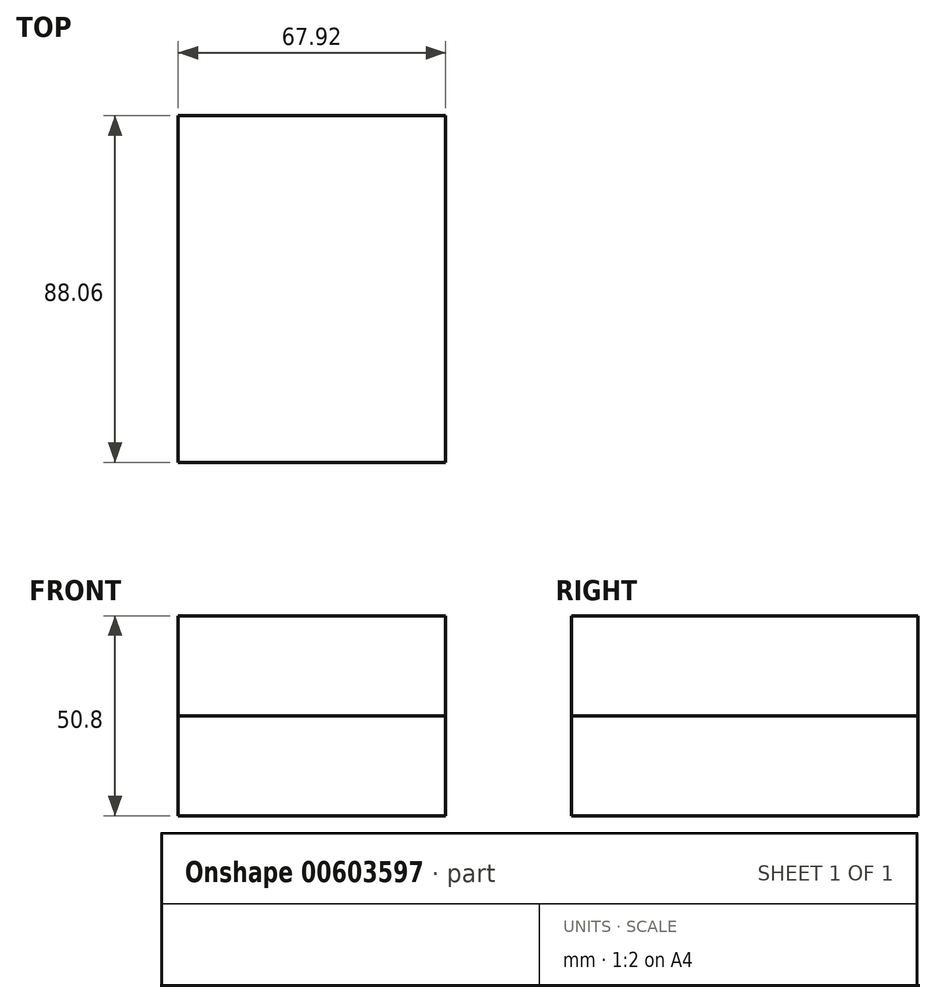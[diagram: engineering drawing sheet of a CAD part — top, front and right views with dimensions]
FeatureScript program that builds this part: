
annotation { "Feature Type Name" : "Feature", "Feature Type Description" : "" }
export const myFeature = defineFeature(function(context is Context, id is Id, definition is map)
    precondition{}
    {
        {
            var Q0;
            Q0=qCreatedBy(makeId("Top.planeOp"),FACE);
            var sketch = newSketch(context, id + "F0", { "sketchPlane" : qUnion([Q0])});
            skLineSegment(sketch, "E0.bottom", {"start": v(33.96, 44.03) * mm, "end": v(-33.96, 44.03) * mm});
            skLineSegment(sketch, "E0.top", {"start": v(33.96, -44.03) * mm, "end": v(-33.96, -44.03) * mm});
            skLineSegment(sketch, "E0.left", {"start": v(33.96, 44.03) * mm, "end": v(33.96, -44.03) * mm});
            skLineSegment(sketch, "E0.right", {"start": v(-33.96, 44.03) * mm, "end": v(-33.96, -44.03) * mm});
            skPoint(sketch, "E0.middle", {"position": v(0, 0) * mm});
            skSolve(sketch);
        }
        {
            var Q0;
            Q0=makeQuery(id+"F0.imprint","IMPRINT",FACE,{"disambiguationData":[TD([[makeQuery(id+"F0.imprint","IMPRINT",EDGE,{"derivedFrom":sQuery(id+"F0.wireOp",EDGE,"E0.bottom")}),1.0]])]});
            extrude(context, id + "F1", {"entities" : qUnion([Q0]), "depth" : 25.4 * mm, "offsetDistance" : 25.4 * mm});
        }
        {
            var Q0;
            Q0=makeQuery(id+"F1.opExtrude","CAP_FACE",FACE,{"disambiguationData":[OSD([sQuery(id+"F0.wireOp",EDGE,"E0.bottom"),sQuery(id+"F0.wireOp",EDGE,"E0.top"),sQuery(id+"F0.wireOp",EDGE,"E0.left"),sQuery(id+"F0.wireOp",EDGE,"E0.right")])],"isStart":true});
            extrude(context, id + "F2", {"entities" : qUnion([Q0]), "operationType" : NewBodyOperationType.ADD, "depth" : 25.4 * mm, "offsetDistance" : 25.4 * mm});
        }
        {
            var Q0;
            Q0=makeQuery(id+"F0.imprint","IMPRINT",FACE,{"disambiguationData":[TD([[makeQuery(id+"F0.imprint","IMPRINT",EDGE,{"derivedFrom":sQuery(id+"F0.wireOp",EDGE,"E0.bottom")}),1.0]])]});
            extrude(context, id + "F3", {"entities" : qUnion([Q0]), "depth" : 25.4 * mm});
        }
    });
